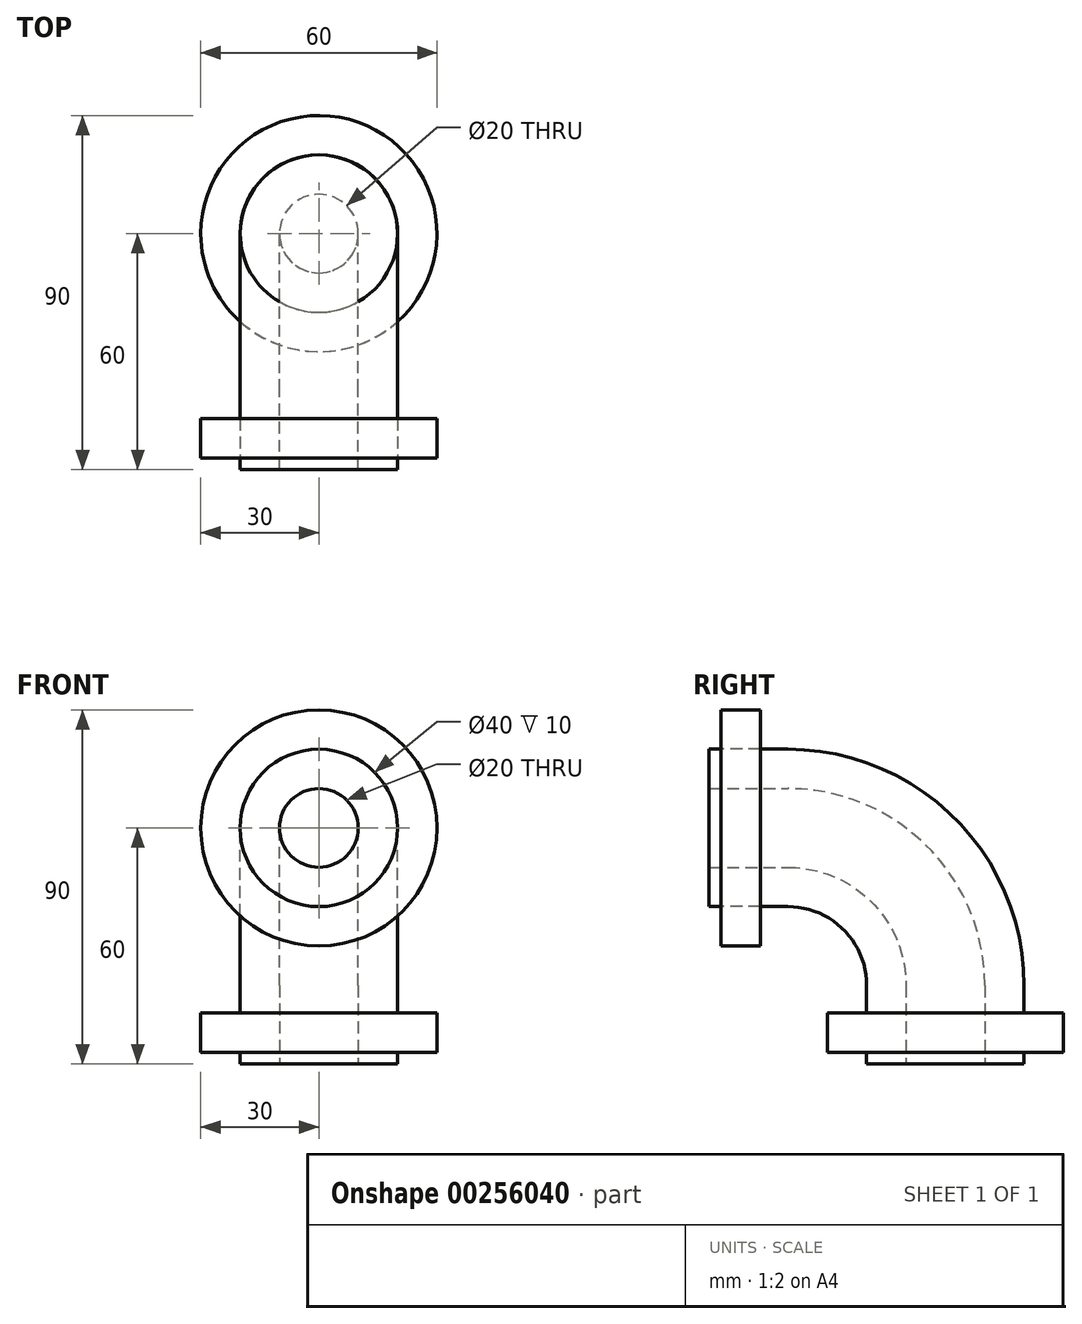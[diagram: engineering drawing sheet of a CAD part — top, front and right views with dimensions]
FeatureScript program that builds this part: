
annotation { "Feature Type Name" : "Feature", "Feature Type Description" : "" }
export const myFeature = defineFeature(function(context is Context, id is Id, definition is map)
    precondition{}
    {
        {
            var Q0;
            Q0=qCreatedBy(makeId("Front.planeOp"),FACE);
            var sketch = newSketch(context, id + "F0", { "sketchPlane" : qUnion([Q0])});
            skCircle(sketch, "E0", {"center": v(0, 0) * mm, "radius": 10 * mm});
            skCircle(sketch, "E1", {"center": v(0, 0) * mm, "radius": 20 * mm});
            skSolve(sketch);
        }
        {
            var Q0;
            Q0=qCreatedBy(makeId("Right.planeOp"),FACE);
            var sketch = newSketch(context, id + "F1", { "sketchPlane" : qUnion([Q0])});
            skLineSegment(sketch, "E2", {"start": v(0, 0) * mm, "end": v(20, 0) * mm});
            skArc(sketch, "E3", {"start": v(60, -40) * mm, "mid": v(48.28, -11.72) * mm, "end": v(20, 0) * mm});
            skLineSegment(sketch, "E4", {"start": v(60, -40) * mm, "end": v(60, -60) * mm});
            skSolve(sketch);
        }
        {
            var Q0;
            Q0=makeQuery(id+"F0.imprint","IMPRINT",FACE,{"disambiguationData":[TD([[makeQuery(id+"F0.imprint","IMPRINT",EDGE,{"derivedFrom":sQuery(id+"F0.wireOp",EDGE,"E0")}),-1.0]])]});
            var Q1;
            Q1=sQuery(id+"F1.wireOp",EDGE,"E2");
            var Q2;
            Q2=sQuery(id+"F1.wireOp",EDGE,"E3");
            var Q3;
            Q3=sQuery(id+"F1.wireOp",EDGE,"E4");
            sweep(context, id + "F2", {"profiles" : qUnion([Q0]), "path" : qUnion([Q1, Q2, Q3])});
        }
        {
            var Q0;
            Q0=makeQuery(id+"F2.opSweep","CAP_FACE",FACE,{"disambiguationData":[OSD([sQuery(id+"F0.wireOp",EDGE,"E0"),sQuery(id+"F0.wireOp",EDGE,"E1"),sQuery(id+"F1.wireOp",VERTEX,"E2.start")])],"isStart":true});
            cPlane(context, id + "F3", {"entities" : qUnion([Q0]), "cplaneType" : CPlaneType.OFFSET, "offset" : 3 * mm, "oppositeDirection" : true, "width" : 150 * mm, "height" : 150 * mm});
        }
        {
            var Q0;
            Q0=qCreatedBy(id+"F3.planeOp",FACE);
            var sketch = newSketch(context, id + "F4", { "sketchPlane" : qUnion([Q0])});
            skCircle(sketch, "E5.0.0", {"center": v(0, 0) * mm, "radius": 20 * mm});
            skCircle(sketch, "E6", {"center": v(0, 0) * mm, "radius": 30 * mm});
            skSolve(sketch);
        }
        {
            var Q0;
            Q0=makeQuery(id+"F4.imprint","IMPRINT",FACE,{"disambiguationData":[TD([[makeQuery(id+"F4.imprint","IMPRINT",EDGE,{"derivedFrom":sQuery(id+"F4.wireOp",EDGE,"E5.0.0")}),-1.0]])]});
            extrude(context, id + "F5", {"entities" : qUnion([Q0]), "oppositeDirection" : true, "depth" : 10 * mm});
        }
        {
            var Q0;
            Q0=makeQuery(id+"F2.opSweep","CAP_FACE",FACE,{"disambiguationData":[OSD([sQuery(id+"F0.wireOp",EDGE,"E0"),sQuery(id+"F0.wireOp",EDGE,"E1"),sQuery(id+"F1.wireOp",VERTEX,"E4.end")])],"isStart":false});
            cPlane(context, id + "F6", {"entities" : qUnion([Q0]), "cplaneType" : CPlaneType.OFFSET, "offset" : 3 * mm, "oppositeDirection" : true, "width" : 150 * mm, "height" : 150 * mm});
        }
        {
            var Q0;
            Q0=qCreatedBy(id+"F6.planeOp",FACE);
            var sketch = newSketch(context, id + "F7", { "sketchPlane" : qUnion([Q0])});
            skCircle(sketch, "E7.0.0", {"center": v(0, -60) * mm, "radius": 20 * mm});
            skCircle(sketch, "E8", {"center": v(0, -60) * mm, "radius": 30 * mm});
            skSolve(sketch);
        }
        {
            var Q0;
            Q0=makeQuery(id+"F2.opSweep","CAP_FACE",FACE,{"disambiguationData":[OSD([sQuery(id+"F0.wireOp",EDGE,"E0"),sQuery(id+"F0.wireOp",EDGE,"E1"),sQuery(id+"F1.wireOp",VERTEX,"E4.end")])],"isStart":false});
            extrude(context, id + "F8", {"entities" : qUnion([Q0]), "operationType" : NewBodyOperationType.ADD, "oppositeDirection" : true, "depth" : 20 * mm});
        }
        {
            var Q0;
            Q0=makeQuery(id+"F7.imprint","IMPRINT",FACE,{"disambiguationData":[TD([[makeQuery(id+"F7.imprint","IMPRINT",EDGE,{"derivedFrom":sQuery(id+"F7.wireOp",EDGE,"E7.0.0")}),-1.0]])]});
            extrude(context, id + "F9", {"entities" : qUnion([Q0]), "operationType" : NewBodyOperationType.ADD, "oppositeDirection" : true, "depth" : 10 * mm});
        }
    });
